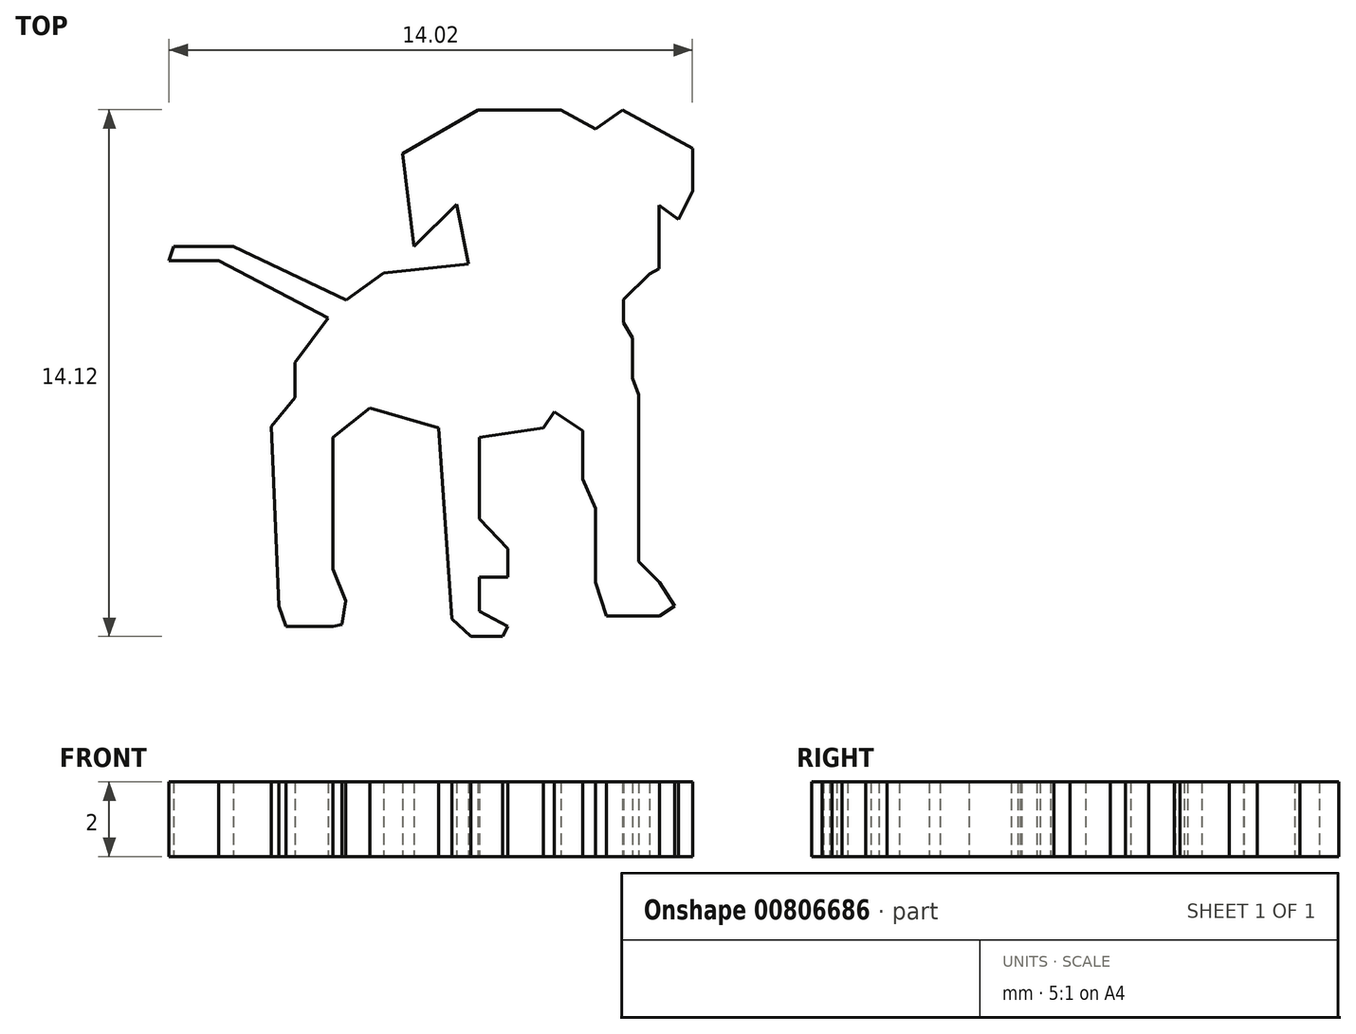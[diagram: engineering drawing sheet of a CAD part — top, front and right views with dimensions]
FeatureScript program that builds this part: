
annotation { "Feature Type Name" : "Feature", "Feature Type Description" : "" }
export const myFeature = defineFeature(function(context is Context, id is Id, definition is map)
    precondition{}
    {
        {
            var Q0;
            Q0=qCreatedBy(makeId("Top.planeOp"),FACE);
            var sketch = newSketch(context, id + "F0", { "sketchPlane" : qUnion([Q0])});
            skLineSegment(sketch, "E0.bottom", {"start": v(0, 0) * mm, "end": v(15, 0) * mm, "construction": true});
            skLineSegment(sketch, "E0.top", {"start": v(0, 15) * mm, "end": v(15, 15) * mm, "construction": true});
            skLineSegment(sketch, "E0.left", {"start": v(0, 0) * mm, "end": v(0, 15) * mm, "construction": true});
            skLineSegment(sketch, "E0.right", {"start": v(15, 0) * mm, "end": v(15, 15) * mm, "construction": true});
            skLineSegment(sketch, "E1", {"start": v(0.54, 10.87) * mm, "end": v(2.13, 10.87) * mm});
            skLineSegment(sketch, "E2", {"start": v(2.13, 10.87) * mm, "end": v(5.15, 9.44) * mm});
            skLineSegment(sketch, "E3", {"start": v(5.15, 9.44) * mm, "end": v(6.15, 10.16) * mm});
            skLineSegment(sketch, "E4", {"start": v(6.15, 10.16) * mm, "end": v(8.43, 10.4) * mm});
            skLineSegment(sketch, "E5", {"start": v(8.43, 10.4) * mm, "end": v(8.11, 12) * mm});
            skLineSegment(sketch, "E6", {"start": v(8.11, 12) * mm, "end": v(6.97, 10.87) * mm});
            skLineSegment(sketch, "E7", {"start": v(6.97, 10.87) * mm, "end": v(6.67, 13.36) * mm});
            skLineSegment(sketch, "E8", {"start": v(6.67, 13.36) * mm, "end": v(8.7, 14.54) * mm});
            skLineSegment(sketch, "E9", {"start": v(8.7, 14.54) * mm, "end": v(10.9, 14.54) * mm});
            skLineSegment(sketch, "E10", {"start": v(10.9, 14.54) * mm, "end": v(11.83, 14.02) * mm});
            skLineSegment(sketch, "E11", {"start": v(11.83, 14.02) * mm, "end": v(12.56, 14.54) * mm});
            skLineSegment(sketch, "E12", {"start": v(12.56, 14.54) * mm, "end": v(14.43, 13.5) * mm});
            skLineSegment(sketch, "E13", {"start": v(14.43, 13.5) * mm, "end": v(14.43, 12.36) * mm});
            skLineSegment(sketch, "E14", {"start": v(14.43, 12.36) * mm, "end": v(14.06, 11.6) * mm});
            skLineSegment(sketch, "E15", {"start": v(14.06, 11.6) * mm, "end": v(13.54, 11.98) * mm});
            skLineSegment(sketch, "E16", {"start": v(13.54, 11.98) * mm, "end": v(13.54, 10.28) * mm});
            skLineSegment(sketch, "E17", {"start": v(13.54, 10.28) * mm, "end": v(13.28, 10.13) * mm});
            skLineSegment(sketch, "E18", {"start": v(13.28, 10.13) * mm, "end": v(12.59, 9.45) * mm});
            skLineSegment(sketch, "E19", {"start": v(12.59, 9.45) * mm, "end": v(12.59, 8.83) * mm});
            skLineSegment(sketch, "E20", {"start": v(12.59, 8.83) * mm, "end": v(12.82, 8.42) * mm});
            skLineSegment(sketch, "E21", {"start": v(12.82, 8.42) * mm, "end": v(12.82, 7.34) * mm});
            skLineSegment(sketch, "E22", {"start": v(12.82, 7.34) * mm, "end": v(13, 6.9) * mm});
            skLineSegment(sketch, "E23", {"start": v(13, 6.9) * mm, "end": v(13, 5.67) * mm});
            skLineSegment(sketch, "E24", {"start": v(13, 5.67) * mm, "end": v(13, 2.43) * mm});
            skLineSegment(sketch, "E25", {"start": v(13, 2.43) * mm, "end": v(13.55, 1.87) * mm});
            skLineSegment(sketch, "E26", {"start": v(13.55, 1.87) * mm, "end": v(13.96, 1.23) * mm});
            skLineSegment(sketch, "E27", {"start": v(13.96, 1.23) * mm, "end": v(13.55, 0.97) * mm});
            skLineSegment(sketch, "E28", {"start": v(13.55, 0.97) * mm, "end": v(12.13, 0.97) * mm});
            skLineSegment(sketch, "E29", {"start": v(12.13, 0.97) * mm, "end": v(11.83, 1.87) * mm});
            skLineSegment(sketch, "E30", {"start": v(11.83, 1.87) * mm, "end": v(11.83, 3.85) * mm});
            skLineSegment(sketch, "E31", {"start": v(11.83, 3.85) * mm, "end": v(11.5, 4.64) * mm});
            skLineSegment(sketch, "E32", {"start": v(11.5, 4.64) * mm, "end": v(11.5, 5.94) * mm});
            skLineSegment(sketch, "E33", {"start": v(11.5, 5.94) * mm, "end": v(10.72, 6.44) * mm});
            skLineSegment(sketch, "E34", {"start": v(10.72, 6.44) * mm, "end": v(10.44, 6) * mm});
            skLineSegment(sketch, "E35", {"start": v(10.44, 6) * mm, "end": v(8.73, 5.76) * mm});
            skLineSegment(sketch, "E36", {"start": v(8.73, 5.76) * mm, "end": v(8.73, 3.57) * mm});
            skLineSegment(sketch, "E37", {"start": v(8.73, 3.57) * mm, "end": v(9.49, 2.77) * mm});
            skLineSegment(sketch, "E38", {"start": v(9.49, 2.77) * mm, "end": v(9.49, 2) * mm});
            skLineSegment(sketch, "E39", {"start": v(9.49, 2) * mm, "end": v(8.73, 2) * mm});
            skLineSegment(sketch, "E40", {"start": v(8.73, 2) * mm, "end": v(8.73, 1.1) * mm});
            skLineSegment(sketch, "E41", {"start": v(8.73, 1.1) * mm, "end": v(9.49, 0.7) * mm});
            skLineSegment(sketch, "E42", {"start": v(9.49, 0.7) * mm, "end": v(9.34, 0.42) * mm});
            skLineSegment(sketch, "E43", {"start": v(9.34, 0.42) * mm, "end": v(8.5, 0.42) * mm});
            skLineSegment(sketch, "E44", {"start": v(8.5, 0.42) * mm, "end": v(7.98, 0.9) * mm});
            skLineSegment(sketch, "E45", {"start": v(7.98, 0.9) * mm, "end": v(7.63, 6) * mm});
            skLineSegment(sketch, "E46", {"start": v(7.63, 6) * mm, "end": v(5.78, 6.54) * mm});
            skLineSegment(sketch, "E47", {"start": v(5.78, 6.54) * mm, "end": v(4.8, 5.76) * mm});
            skLineSegment(sketch, "E48", {"start": v(4.8, 5.76) * mm, "end": v(4.8, 2.22) * mm});
            skLineSegment(sketch, "E49", {"start": v(4.8, 2.22) * mm, "end": v(5.14, 1.38) * mm});
            skLineSegment(sketch, "E50", {"start": v(5.04, 0.74) * mm, "end": v(5.14, 1.38) * mm});
            skLineSegment(sketch, "E51", {"start": v(5.04, 0.74) * mm, "end": v(4.8, 0.7) * mm});
            skLineSegment(sketch, "E52", {"start": v(4.8, 0.7) * mm, "end": v(3.55, 0.7) * mm});
            skLineSegment(sketch, "E53", {"start": v(3.55, 0.7) * mm, "end": v(3.35, 1.23) * mm});
            skLineSegment(sketch, "E54", {"start": v(3.35, 1.23) * mm, "end": v(3.14, 6.05) * mm});
            skLineSegment(sketch, "E55", {"start": v(3.14, 6.05) * mm, "end": v(3.78, 6.82) * mm});
            skLineSegment(sketch, "E56", {"start": v(3.78, 6.82) * mm, "end": v(3.78, 7.76) * mm});
            skLineSegment(sketch, "E57", {"start": v(3.78, 7.76) * mm, "end": v(4.67, 8.96) * mm});
            skLineSegment(sketch, "E58", {"start": v(4.67, 8.96) * mm, "end": v(1.74, 10.5) * mm});
            skLineSegment(sketch, "E59", {"start": v(1.74, 10.5) * mm, "end": v(0.4, 10.5) * mm});
            skLineSegment(sketch, "E60", {"start": v(0.4, 10.5) * mm, "end": v(0.54, 10.87) * mm});
            skSolve(sketch);
        }
        {
            var Q0;
            Q0 = qSketchRegion(id + "F0", true);
            extrude(context, id + "F1", {"entities" : qUnion([Q0]), "depth" : 2 * mm, "offsetDistance" : 25 * mm});
        }
    });
